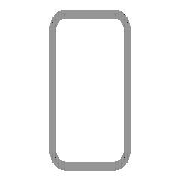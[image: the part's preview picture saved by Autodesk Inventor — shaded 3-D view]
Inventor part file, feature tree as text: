
AUTODESK INVENTOR PART (.ipt)
format: ipt  version: 2025 (Build 290162010, 162A)  size: 138,752 bytes
history: native  units: mm (DEFAULTED — no unit token found)
features: other x3, sketch x1, plane x1
ambient origin geometry x8: Origin, YZ Plane, XZ Plane, XY Plane, X Axis, Y Axis, Z Axis, Center Point
bodies: Solid1 (feature_tree), Body (feature_tree)
feature tree (5):
  other  "Driven Length"
  other  "Start plane"
  other  "End plane"
  sketch  "Sketch3"  dims[d3=0.001mm d4=0.0mm d7=4.5mm d10=80.0mm d11=40.0mm d12=3.0mm d13=-0.0mm d14=0.001mm d15=40.0mm d16=20.0mm d17=90.0deg d18=0.001mm d19=3.0mm d20=3.0mm]
  plane  "Work Plane3"
